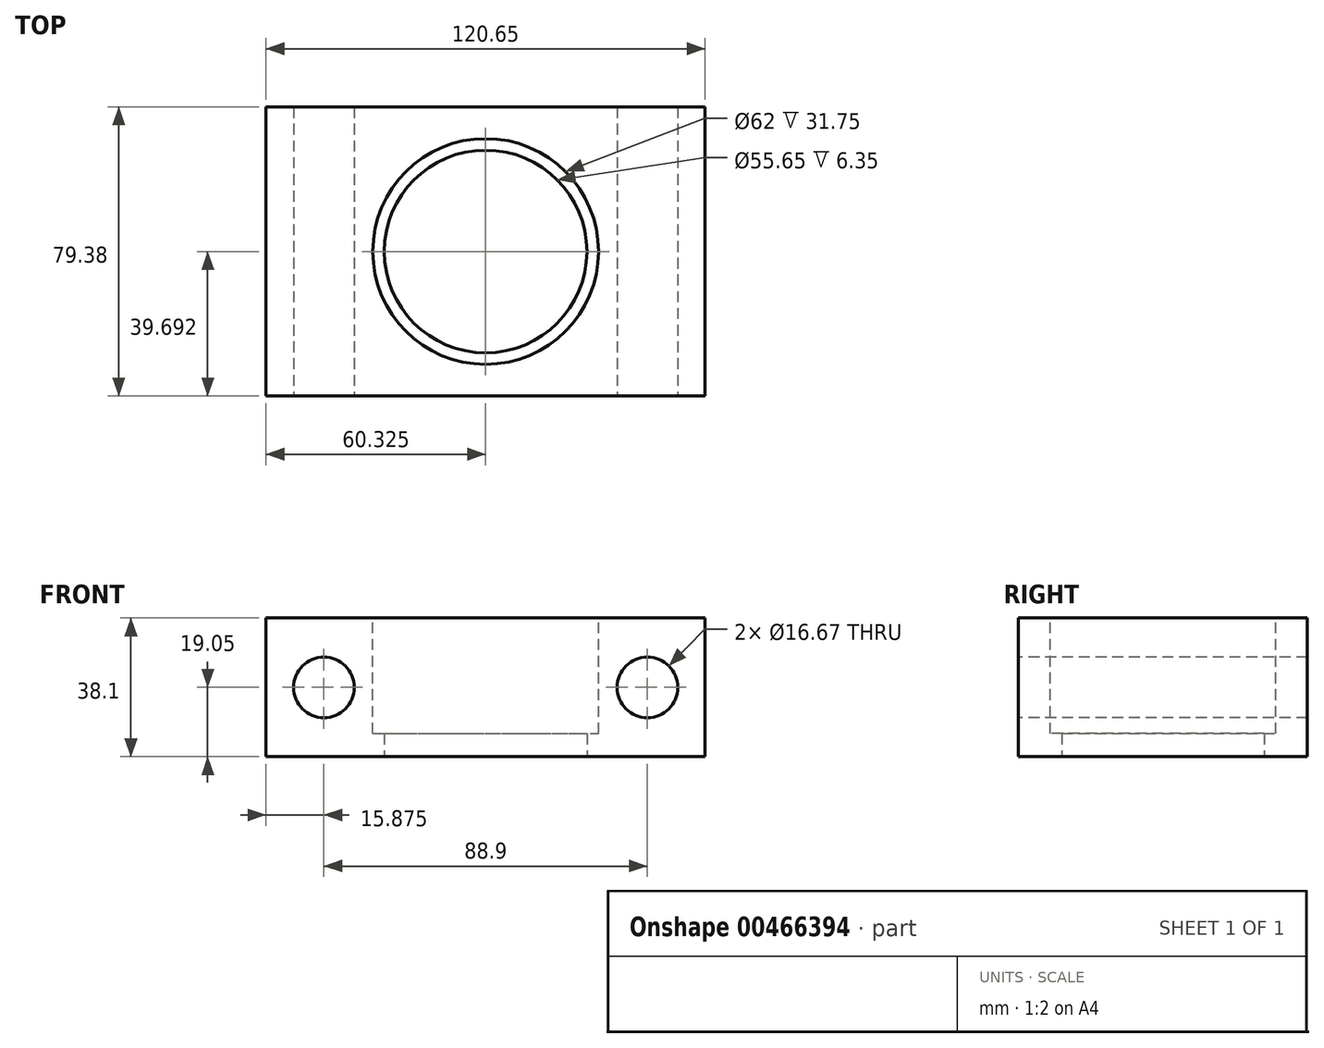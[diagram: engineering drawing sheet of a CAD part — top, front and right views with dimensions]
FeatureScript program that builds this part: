
annotation { "Feature Type Name" : "Feature", "Feature Type Description" : "" }
export const myFeature = defineFeature(function(context is Context, id is Id, definition is map)
    precondition{}
    {
        {
            var Q0;
            Q0=qCreatedBy(makeId("Front.planeOp"),FACE);
            var sketch = newSketch(context, id + "F0", { "sketchPlane" : qUnion([Q0])});
            skLineSegment(sketch, "E0.bottom", {"start": v(0, 0) * mm, "end": v(120.65, 0) * mm});
            skLineSegment(sketch, "E0.top", {"start": v(0, 38.1) * mm, "end": v(120.65, 38.1) * mm});
            skLineSegment(sketch, "E0.left", {"start": v(0, 0) * mm, "end": v(0, 38.1) * mm});
            skLineSegment(sketch, "E0.right", {"start": v(120.65, 0) * mm, "end": v(120.65, 38.1) * mm});
            skSolve(sketch);
        }
        {
            var Q0;
            Q0 = qSketchRegion(id + "F0", true);
            extrude(context, id + "F1", {"entities" : qUnion([Q0]), "depth" : 79.38 * mm, "offsetDistance" : 25.4 * mm});
        }
        {
            var Q0;
            Q0=makeQuery(id+"F1.opExtrude","SWEPT_FACE",FACE,{"disambiguationData":[OSD([sQuery(id+"F0.wireOp",EDGE,"E0.top")])]});
            var sketch = newSketch(context, id + "F2", { "sketchPlane" : qUnion([Q0])});
            skLineSegment(sketch, "E1", {"start": v(0, -39.69) * mm, "end": v(120.65, -39.69) * mm, "construction": true});
            skCircle(sketch, "E2", {"center": v(60.32, -39.69) * mm, "radius": 31 * mm});
            skSolve(sketch);
        }
        {
            var Q0;
            Q0 = qSketchRegion(id + "F2", true);
            extrude(context, id + "F3", {"entities" : qUnion([Q0]), "operationType" : NewBodyOperationType.REMOVE, "endBound" : BoundingType.THROUGH_ALL, "oppositeDirection" : true, "depth" : 25.4 * mm});
        }
        {
            var Q0;
            Q0=makeQuery(id+"F1.opExtrude","SWEPT_FACE",FACE,{"disambiguationData":[OSD([sQuery(id+"F0.wireOp",EDGE,"E0.bottom")])]});
            var sketch = newSketch(context, id + "F4", { "sketchPlane" : qUnion([Q0])});
            skCircle(sketch, "E3.0", {"center": v(60.32, 39.69) * mm, "radius": 31 * mm});
            skCircle(sketch, "E4.0", {"center": v(60.32, 39.69) * mm, "radius": 27.83 * mm});
            skSolve(sketch);
        }
        {
            var Q0;
            Q0 = qSketchRegion(id + "F4", true);
            extrude(context, id + "F5", {"entities" : qUnion([Q0]), "operationType" : NewBodyOperationType.ADD, "oppositeDirection" : true, "depth" : 6.35 * mm, "offsetDistance" : 25.4 * mm});
        }
        {
            var Q0;
            Q0=makeQuery(id+"F1.opExtrude","CAP_FACE",FACE,{"disambiguationData":[OSD([sQuery(id+"F0.wireOp",EDGE,"E0.bottom"),sQuery(id+"F0.wireOp",EDGE,"E0.top"),sQuery(id+"F0.wireOp",EDGE,"E0.left"),sQuery(id+"F0.wireOp",EDGE,"E0.right")])],"isStart":false});
            var sketch = newSketch(context, id + "F6", { "sketchPlane" : qUnion([Q0])});
            skLineSegment(sketch, "E5", {"start": v(0, 19.05) * mm, "end": v(120.65, 19.05) * mm, "construction": true});
            skCircle(sketch, "E6", {"center": v(15.88, 19.05) * mm, "radius": 8.33 * mm});
            skCircle(sketch, "E7", {"center": v(104.77, 19.05) * mm, "radius": 8.33 * mm});
            skSolve(sketch);
        }
        {
            var Q0;
            Q0 = qSketchRegion(id + "F6", true);
            extrude(context, id + "F7", {"entities" : qUnion([Q0]), "operationType" : NewBodyOperationType.REMOVE, "endBound" : BoundingType.THROUGH_ALL, "oppositeDirection" : true, "depth" : 25.4 * mm, "offsetDistance" : 25.4 * mm});
        }
    });
